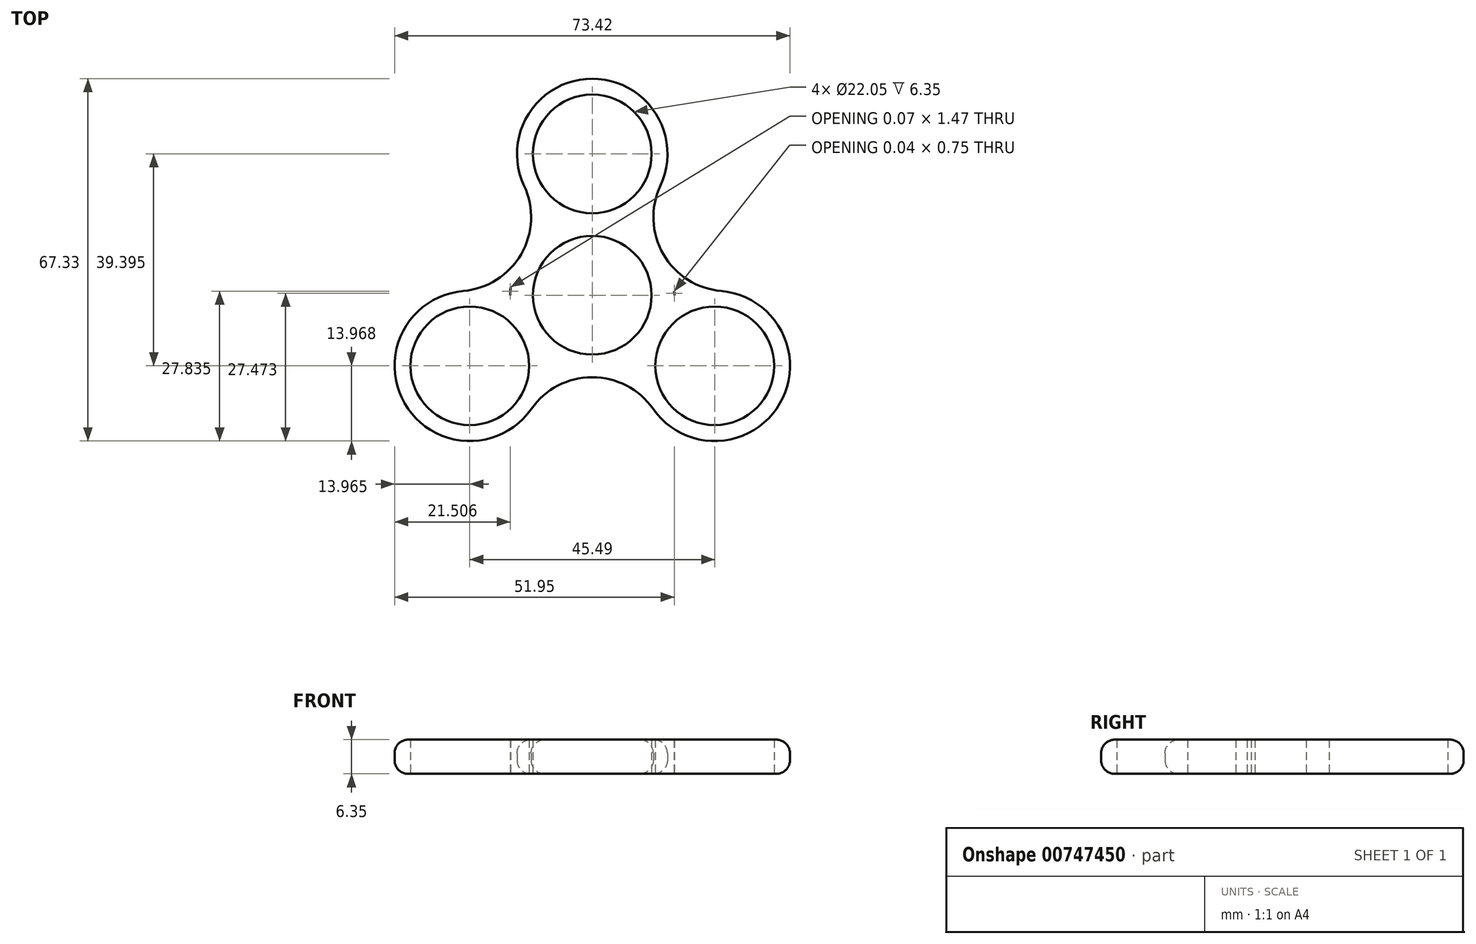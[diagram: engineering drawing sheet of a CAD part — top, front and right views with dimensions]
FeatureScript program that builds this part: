
annotation { "Feature Type Name" : "Feature", "Feature Type Description" : "" }
export const myFeature = defineFeature(function(context is Context, id is Id, definition is map)
    precondition{}
    {
        {
            var Q0;
            Q0=qCreatedBy(makeId("Top.planeOp"),FACE);
            var sketch = newSketch(context, id + "F0", { "sketchPlane" : qUnion([Q0])});
            skCircle(sketch, "E0", {"center": v(0, 0) * mm, "radius": 11.02 * mm});
            skArc(sketch, "E1", {"start": v(8.8, -12.45) * mm, "mid": v(11.26, -10.27) * mm, "end": v(13.2, -7.62) * mm});
            skCircle(sketch, "E2", {"center": v(0, 26.26) * mm, "radius": 13.97 * mm});
            skCircle(sketch, "E3", {"center": v(0, 26.26) * mm, "radius": 11.02 * mm});
            skLineSegment(sketch, "E4", {"start": v(0, 26.26) * mm, "end": v(13.97, 26.26) * mm});
            skLineSegment(sketch, "E5", {"start": v(15.26, 0) * mm, "end": v(-15.24, 0) * mm});
            skLineSegment(sketch, "E6", {"start": v(0, 26.26) * mm, "end": v(-13.97, 26.26) * mm});
            skLineSegment(sketch, "E7", {"start": v(-14.99, 5.18) * mm, "end": v(-15.24, 0) * mm});
            skArc(sketch, "E8", {"start": v(-23.94, 0.79) * mm, "mid": v(-13.2, 7.62) * mm, "end": v(-12.65, 20.34) * mm});
            skArc(sketch, "E9", {"start": v(12.65, 20.34) * mm, "mid": v(13.2, 7.62) * mm, "end": v(23.94, 0.79) * mm});
            skCircle(sketch, "E10.1.0", {"center": v(-22.74, -13.13) * mm, "radius": 13.97 * mm});
            skCircle(sketch, "E10.1.1", {"center": v(-22.74, -13.13) * mm, "radius": 11.02 * mm});
            skCircle(sketch, "E10.2.0", {"center": v(22.74, -13.13) * mm, "radius": 13.97 * mm});
            skCircle(sketch, "E10.2.1", {"center": v(22.74, -13.13) * mm, "radius": 11.02 * mm});
            skArc(sketch, "E11", {"start": v(11.29, -21.13) * mm, "mid": v(0, -15.24) * mm, "end": v(-11.29, -21.13) * mm});
            skArc(sketch, "E12.trimOffspring", {"start": v(-15.17, 1.47) * mm, "mid": v(-15.24, 0.04) * mm, "end": v(-15.18, -1.39) * mm});
            skLineSegment(sketch, "E13.trimOffspring", {"start": v(15.22, 0.75) * mm, "end": v(15.26, 0) * mm});
            skArc(sketch, "E14.trimOffspring", {"start": v(15.18, -1.39) * mm, "mid": v(15.24, -0.32) * mm, "end": v(15.22, 0.75) * mm});
            skSolve(sketch);
        }
        {
            var Q0;
            {var subQ0=sQuery(id+"F0.wireOp",EDGE,"E4");var subQ1=sQuery(id+"F0.wireOp",EDGE,"E2");var subQ2=makeQuery(id+"F0.imprint","INTERSECT",VERTEX,{"derivedFrom":[subQ1,subQ0]});Q0=makeQuery(id+"F0.imprint","IMPRINT",FACE,{"disambiguationData":[TD([[makeQuery(id+"F0.imprint","IMPRINT",EDGE,{"disambiguationData":[TD([[subQ2,-1.0]])],"derivedFrom":subQ1}),1.0]])]});}
            var Q1;
            {var subQ3=sQuery(id+"F0.wireOp",EDGE,"E6");var subQ5=sQuery(id+"F0.wireOp",EDGE,"E2");var subQ9=makeQuery(id+"F0.imprint","INTERSECT",VERTEX,{"derivedFrom":[subQ5,subQ3]});Q1=makeQuery(id+"F0.imprint","IMPRINT",FACE,{"disambiguationData":[TD([[makeQuery(id+"F0.imprint","IMPRINT",EDGE,{"disambiguationData":[TD([[subQ9,-1.0]])],"derivedFrom":subQ5}),1.0]])]});}
            var Q2;
            {var subQ1=sQuery(id+"F0.wireOp",EDGE,"E9");Q2=makeQuery(id+"F0.imprint","IMPRINT",FACE,{"disambiguationData":[TD([[makeQuery(id+"F0.imprint","IMPRINT",EDGE,{"derivedFrom":subQ1}),-1.0]])]});}
            var Q3;
            {var subQ1=sQuery(id+"F0.wireOp",EDGE,"E8");var subQ5=sQuery(id+"F0.wireOp",EDGE,"E7");var subQ6=makeQuery(id+"F0.imprint","INTERSECT",VERTEX,{"derivedFrom":[subQ5,subQ1]});Q3=makeQuery(id+"F0.imprint","IMPRINT",FACE,{"disambiguationData":[TD([[makeQuery(id+"F0.imprint","IMPRINT",EDGE,{"disambiguationData":[TD([[subQ6,-1.0]])],"derivedFrom":subQ5}),-1.0]])]});}
            var Q4;
            Q4=makeQuery(id+"F0.imprint","IMPRINT",FACE,{"disambiguationData":[TD([[makeQuery(id+"F0.imprint","IMPRINT",EDGE,{"derivedFrom":sQuery(id+"F0.wireOp",EDGE,"E10.1.1")}),-1.0]])]});
            var Q5;
            {var subQ5=sQuery(id+"F0.wireOp",EDGE,"E11");Q5=makeQuery(id+"F0.imprint","IMPRINT",FACE,{"disambiguationData":[TD([[makeQuery(id+"F0.imprint","IMPRINT",EDGE,{"derivedFrom":subQ5}),-1.0]])]});}
            var Q6;
            Q6=makeQuery(id+"F0.imprint","IMPRINT",FACE,{"disambiguationData":[TD([[makeQuery(id+"F0.imprint","IMPRINT",EDGE,{"derivedFrom":sQuery(id+"F0.wireOp",EDGE,"E10.2.1")}),-1.0]])]});
            extrude(context, id + "F1", {"entities" : qUnion([Q0, Q1, Q2, Q3, Q4, Q5, Q6]), "depth" : 6.35 * mm, "offsetDistance" : 25.4 * mm});
        }
        {
            var Q0;
            Q0=makeQuery(id+"F1.opExtrude","CAP_EDGE",EDGE,{"disambiguationData":[OSD([sQuery(id+"F0.wireOp",EDGE,"E2")])],"isStart":false});
            var Q1;
            Q1=makeQuery(id+"F1.opExtrude","CAP_EDGE",EDGE,{"disambiguationData":[OSD([sQuery(id+"F0.wireOp",EDGE,"E8")])],"isStart":false});
            var Q2;
            Q2=makeQuery(id+"F1.opExtrude","CAP_EDGE",EDGE,{"disambiguationData":[OSD([sQuery(id+"F0.wireOp",EDGE,"E10.1.0")])],"isStart":false});
            var Q3;
            Q3=makeQuery(id+"F1.opExtrude","CAP_EDGE",EDGE,{"disambiguationData":[OSD([sQuery(id+"F0.wireOp",EDGE,"E11")])],"isStart":false});
            var Q4;
            Q4=makeQuery(id+"F1.opExtrude","CAP_EDGE",EDGE,{"disambiguationData":[OSD([sQuery(id+"F0.wireOp",EDGE,"E10.2.0")])],"isStart":false});
            var Q5;
            Q5=makeQuery(id+"F1.opExtrude","CAP_EDGE",EDGE,{"disambiguationData":[OSD([sQuery(id+"F0.wireOp",EDGE,"E9")])],"isStart":false});
            var Q6;
            Q6=makeQuery(id+"F1.opExtrude","SWEPT_FACE",FACE,{"disambiguationData":[OSD([sQuery(id+"F0.wireOp",EDGE,"E10.1.0")])]});
            var Q7;
            Q7=makeQuery(id+"F1.opExtrude","SWEPT_FACE",FACE,{"disambiguationData":[OSD([sQuery(id+"F0.wireOp",EDGE,"E11")])]});
            var Q8;
            Q8=makeQuery(id+"F1.opExtrude","SWEPT_FACE",FACE,{"disambiguationData":[OSD([sQuery(id+"F0.wireOp",EDGE,"E10.2.0")])]});
            var Q9;
            Q9=makeQuery(id+"F1.opExtrude","SWEPT_FACE",FACE,{"disambiguationData":[OSD([sQuery(id+"F0.wireOp",EDGE,"E9")])]});
            var Q10;
            Q10=makeQuery(id+"F1.opExtrude","CAP_EDGE",EDGE,{"disambiguationData":[OSD([sQuery(id+"F0.wireOp",EDGE,"E2")])],"isStart":true});
            var Q11;
            Q11=makeQuery(id+"F1.opExtrude","CAP_EDGE",EDGE,{"disambiguationData":[OSD([sQuery(id+"F0.wireOp",EDGE,"E8")])],"isStart":true});
            fillet(context, id + "F2", {"entities" : qUnion([Q0, Q1, Q2, Q3, Q4, Q5, Q6, Q7, Q8, Q9, Q10, Q11]), "radius" : 2.54 * mm, "tangentPropagation" : true, "allowEdgeOverflow" : false});
        }
    });
